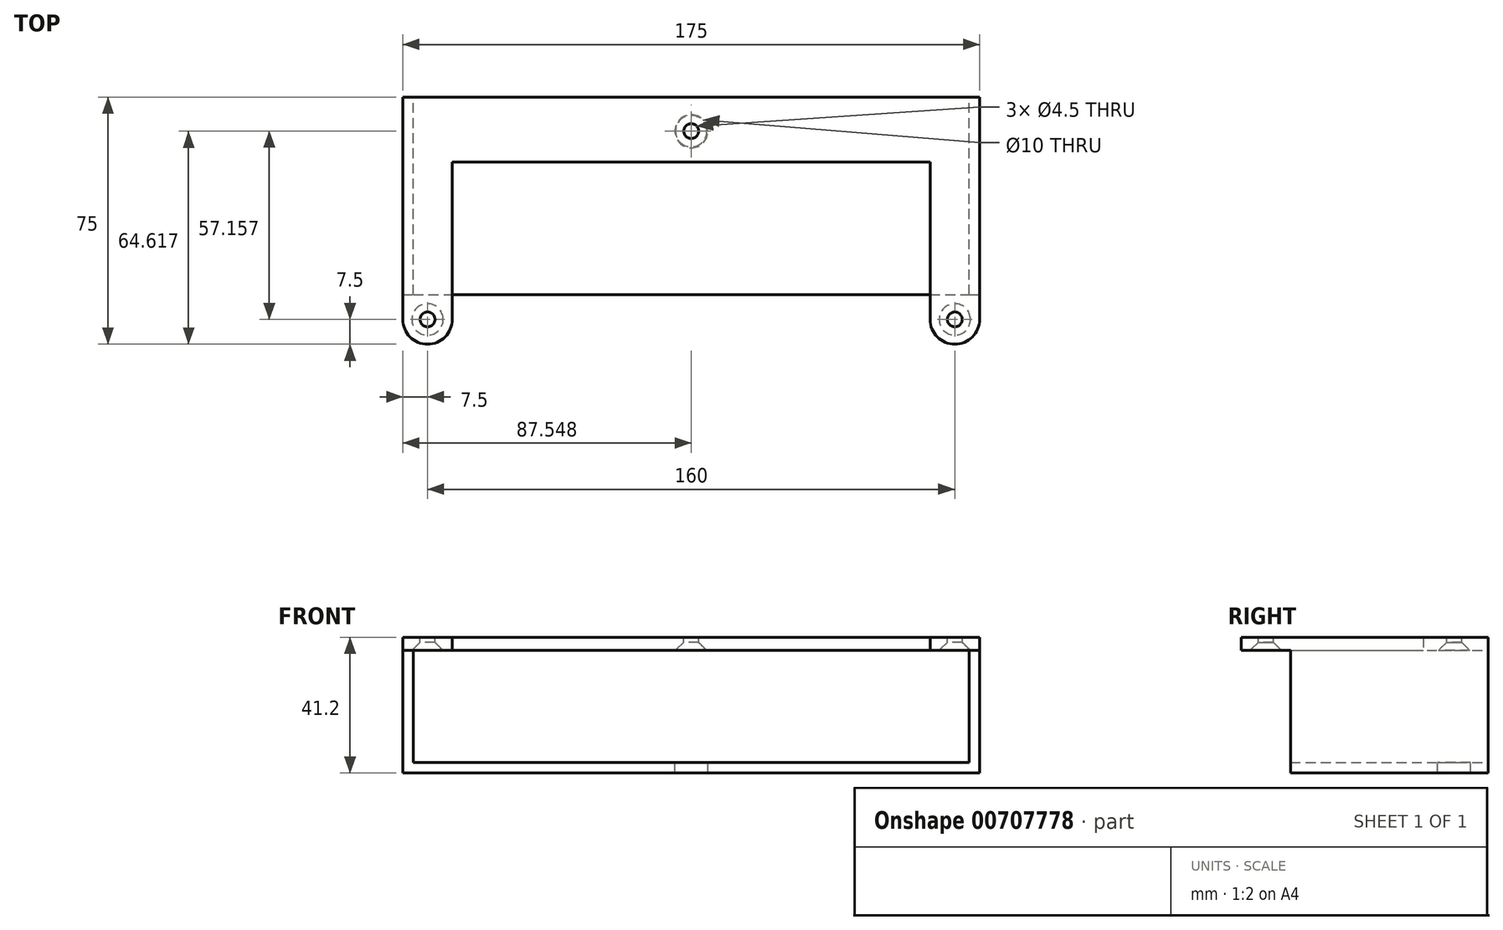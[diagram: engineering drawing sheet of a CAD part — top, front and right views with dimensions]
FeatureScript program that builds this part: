
annotation { "Feature Type Name" : "Feature", "Feature Type Description" : "" }
export const myFeature = defineFeature(function(context is Context, id is Id, definition is map)
    precondition{}
    {
        {
            var Q0;
            Q0=qCreatedBy(makeId("Top.planeOp"),FACE);
            var sketch = newSketch(context, id + "F0", { "sketchPlane" : qUnion([Q0])});
            skLineSegment(sketch, "E0.bottom", {"start": v(0, 0) * mm, "end": v(175, 0) * mm});
            skLineSegment(sketch, "E0.top", {"start": v(0, -60) * mm, "end": v(175, -60) * mm});
            skLineSegment(sketch, "E0.left", {"start": v(0, 0) * mm, "end": v(0, -60) * mm});
            skLineSegment(sketch, "E0.right", {"start": v(175, 0) * mm, "end": v(175, -60) * mm});
            skLineSegment(sketch, "E1", {"start": v(3.2, -60) * mm, "end": v(3.2, 0) * mm});
            skLineSegment(sketch, "E2", {"start": v(171.8, -60) * mm, "end": v(171.8, 0) * mm});
            skSolve(sketch);
        }
        {
            var Q0;
            Q0 = qSketchRegion(id + "F0", true);
            extrude(context, id + "F1", {"entities" : qUnion([Q0]), "depth" : 3 * mm, "offsetDistance" : 25 * mm});
        }
        {
            var Q0;
            {var subQ0=sQuery(id+"F0.wireOp",EDGE,"E0.left");Q0=makeQuery(id+"F0.imprint","IMPRINT",FACE,{"disambiguationData":[TD([[makeQuery(id+"F0.imprint","IMPRINT",EDGE,{"derivedFrom":subQ0}),1.0]])]});}
            var Q1;
            {var subQ0=sQuery(id+"F0.wireOp",EDGE,"E0.right");Q1=makeQuery(id+"F0.imprint","IMPRINT",FACE,{"disambiguationData":[TD([[makeQuery(id+"F0.imprint","IMPRINT",EDGE,{"derivedFrom":subQ0}),-1.0]])]});}
            extrude(context, id + "F2", {"entities" : qUnion([Q0, Q1]), "operationType" : NewBodyOperationType.ADD, "oppositeDirection" : true, "depth" : 37.2 * mm, "offsetDistance" : 25 * mm});
        }
        {
            var Q0;
            Q0=makeQuery(id+"F2.opExtrude","SWEPT_FACE",FACE,{"disambiguationData":[OSD([sQuery(id+"F0.wireOp",EDGE,"E2")])]});
            var sketch = newSketch(context, id + "F3", { "sketchPlane" : qUnion([Q0])});
            skLineSegment(sketch, "E3.bottom", {"start": v(60, -37.2) * mm, "end": v(0, -37.2) * mm});
            skLineSegment(sketch, "E3.top", {"start": v(60, -34) * mm, "end": v(0, -34) * mm});
            skLineSegment(sketch, "E3.left", {"start": v(60, -37.2) * mm, "end": v(60, -34) * mm});
            skLineSegment(sketch, "E3.right", {"start": v(0, -37.2) * mm, "end": v(0, -34) * mm});
            skSolve(sketch);
        }
        {
            var Q0;
            Q0 = qSketchRegion(id + "F3", true);
            var Q1;
            Q1=makeQuery(id+"F2.opExtrude","SWEPT_FACE",FACE,{"disambiguationData":[OSD([sQuery(id+"F0.wireOp",EDGE,"E1")])]});
            extrude(context, id + "F4", {"entities" : qUnion([Q0]), "operationType" : NewBodyOperationType.ADD, "endBound" : BoundingType.UP_TO_SURFACE, "depth" : 25 * mm, "endBoundEntityFace" : qUnion([Q1]), "offsetDistance" : 25 * mm});
        }
        {
            var Q0;
            {var subQ0=sQuery(id+"F0.wireOp",EDGE,"E0.top");Q0=makeQuery(id+"F4.boolean.opBoolean","MERGE",FACE,{"derivedFrom":[makeQuery(id+"F2.boolean.opBoolean","MERGE",FACE,{"derivedFrom":[makeQuery(id+"F1.opExtrude","SWEPT_FACE",FACE,{"disambiguationData":[OSD([subQ0])]}),makeQuery(id+"F2.opExtrude","SWEPT_FACE",FACE,{"disambiguationData":[OSD([subQ0]),TDD([makeQuery(id+"F0.imprint","IMPRINT",EDGE,{"disambiguationData":[TD([[makeQuery(id+"F0.imprint","INTERSECT",VERTEX,{"derivedFrom":[subQ0,sQuery(id+"F0.wireOp",EDGE,"E0.left")]}),-1.0]])],"derivedFrom":subQ0})])]}),makeQuery(id+"F2.opExtrude","SWEPT_FACE",FACE,{"disambiguationData":[OSD([subQ0]),TDD([makeQuery(id+"F0.imprint","IMPRINT",EDGE,{"disambiguationData":[TD([[makeQuery(id+"F0.imprint","INTERSECT",VERTEX,{"derivedFrom":[subQ0,sQuery(id+"F0.wireOp",EDGE,"E0.right")]}),1.0]])],"derivedFrom":subQ0})])]})]}),makeQuery(id+"F4.opExtrude","SWEPT_FACE",FACE,{"disambiguationData":[OSD([sQuery(id+"F3.wireOp",EDGE,"E3.left")])]})]});}
            var sketch = newSketch(context, id + "F5", { "sketchPlane" : qUnion([Q0])});
            skLineSegment(sketch, "E4", {"start": v(87.5, 3) * mm, "end": v(87.5, 0) * mm, "construction": true});
            skLineSegment(sketch, "E5.bottom", {"start": v(0, 3) * mm, "end": v(15, 3) * mm});
            skLineSegment(sketch, "E5.top", {"start": v(0, 0) * mm, "end": v(15, 0) * mm});
            skLineSegment(sketch, "E5.left", {"start": v(0, 3) * mm, "end": v(0, 0) * mm});
            skLineSegment(sketch, "E5.right", {"start": v(15, 3) * mm, "end": v(15, 0) * mm});
            skLineSegment(sketch, "E6.MirrorCS", {"start": v(175, 3) * mm, "end": v(175, 0) * mm});
            skLineSegment(sketch, "E7.MirrorCS", {"start": v(160, 3) * mm, "end": v(160, 0) * mm});
            skLineSegment(sketch, "E8.MirrorCS", {"start": v(175, 3) * mm, "end": v(160, 3) * mm});
            skLineSegment(sketch, "E9.MirrorCS", {"start": v(175, 0) * mm, "end": v(160, 0) * mm});
            skSolve(sketch);
        }
        {
            var Q0;
            Q0 = qSketchRegion(id + "F5", true);
            extrude(context, id + "F6", {"entities" : qUnion([Q0]), "operationType" : NewBodyOperationType.ADD, "depth" : 15 * mm, "offsetDistance" : 25 * mm});
        }
        {
            var Q0;
            {var subQ0=sQuery(id+"F0.wireOp",EDGE,"E0.bottom");Q0=makeQuery(id+"F4.boolean.opBoolean","MERGE",FACE,{"derivedFrom":[makeQuery(id+"F2.boolean.opBoolean","MERGE",FACE,{"derivedFrom":[makeQuery(id+"F1.opExtrude","SWEPT_FACE",FACE,{"disambiguationData":[OSD([subQ0])]}),makeQuery(id+"F2.opExtrude","SWEPT_FACE",FACE,{"disambiguationData":[OSD([subQ0]),TDD([makeQuery(id+"F0.imprint","IMPRINT",EDGE,{"disambiguationData":[TD([[makeQuery(id+"F0.imprint","INTERSECT",VERTEX,{"derivedFrom":[subQ0,sQuery(id+"F0.wireOp",EDGE,"E0.left")]}),-1.0]])],"derivedFrom":subQ0})])]}),makeQuery(id+"F2.opExtrude","SWEPT_FACE",FACE,{"disambiguationData":[OSD([subQ0]),TDD([makeQuery(id+"F0.imprint","IMPRINT",EDGE,{"disambiguationData":[TD([[makeQuery(id+"F0.imprint","INTERSECT",VERTEX,{"derivedFrom":[subQ0,sQuery(id+"F0.wireOp",EDGE,"E0.right")]}),1.0]])],"derivedFrom":subQ0})])]})]}),makeQuery(id+"F4.opExtrude","SWEPT_FACE",FACE,{"disambiguationData":[OSD([sQuery(id+"F3.wireOp",EDGE,"E3.right")])]})]});}
            var sketch = newSketch(context, id + "F7", { "sketchPlane" : qUnion([Q0])});
            skLineSegment(sketch, "E10", {"start": v(-87.5, 3) * mm, "end": v(-87.5, 0) * mm, "construction": true});
            skLineSegment(sketch, "E11.bottom", {"start": v(-175, 3) * mm, "end": v(-160, 3) * mm});
            skLineSegment(sketch, "E11.top", {"start": v(-175, 0) * mm, "end": v(-160, 0) * mm});
            skLineSegment(sketch, "E11.left", {"start": v(-175, 3) * mm, "end": v(-175, 0) * mm});
            skLineSegment(sketch, "E11.right", {"start": v(-160, 3) * mm, "end": v(-160, 0) * mm});
            skLineSegment(sketch, "E12.MirrorCS", {"start": v(0, 3) * mm, "end": v(0, 0) * mm});
            skLineSegment(sketch, "E13.MirrorCS", {"start": v(-15, 3) * mm, "end": v(-15, 0) * mm});
            skLineSegment(sketch, "E14.MirrorCS", {"start": v(0, 3) * mm, "end": v(-15, 3) * mm});
            skLineSegment(sketch, "E15.MirrorCS", {"start": v(0, 0) * mm, "end": v(-15, 0) * mm});
            skSolve(sketch);
        }
        {
            var Q0;
            Q0 = qSketchRegion(id + "F7", true);
            extrude(context, id + "F8", {"entities" : qUnion([Q0]), "operationType" : NewBodyOperationType.ADD, "depth" : 15 * mm, "offsetDistance" : 25 * mm});
        }
        {
            var Q0;
            Q0=makeQuery(id+"F8.boolean.opBoolean","MERGE",FACE,{"derivedFrom":[makeQuery(id+"F6.boolean.opBoolean","MERGE",FACE,{"derivedFrom":[makeQuery(id+"F1.opExtrude","CAP_FACE",FACE,{"disambiguationData":[OSD([sQuery(id+"F0.wireOp",EDGE,"E0.bottom"),sQuery(id+"F0.wireOp",EDGE,"E0.top"),sQuery(id+"F0.wireOp",EDGE,"E0.left"),sQuery(id+"F0.wireOp",EDGE,"E0.right")])],"isStart":false}),makeQuery(id+"F6.opExtrude","SWEPT_FACE",FACE,{"disambiguationData":[OSD([sQuery(id+"F5.wireOp",EDGE,"E5.bottom")])]}),makeQuery(id+"F6.opExtrude","SWEPT_FACE",FACE,{"disambiguationData":[OSD([sQuery(id+"F5.wireOp",EDGE,"E8.MirrorCS")])]})]}),makeQuery(id+"F8.opExtrude","SWEPT_FACE",FACE,{"disambiguationData":[OSD([sQuery(id+"F7.wireOp",EDGE,"E11.bottom")])]}),makeQuery(id+"F8.opExtrude","SWEPT_FACE",FACE,{"disambiguationData":[OSD([sQuery(id+"F7.wireOp",EDGE,"E14.MirrorCS")])]})]});
            var sketch = newSketch(context, id + "F9", { "sketchPlane" : qUnion([Q0])});
            skCircle(sketch, "E16", {"center": v(167.5, 7.5) * mm, "radius": 2.25 * mm});
            skCircle(sketch, "E17", {"center": v(167.5, -67.5) * mm, "radius": 2.25 * mm});
            skCircle(sketch, "E18", {"center": v(7.5, -67.5) * mm, "radius": 2.25 * mm});
            skCircle(sketch, "E19", {"center": v(87.5, -10.34) * mm, "radius": 2.25 * mm});
            skPoint(sketch, "E20", {"position": v(87.5, 0) * mm});
            skSolve(sketch);
        }
        {
            var Q0;
            Q0 = qSketchRegion(id + "F9", true);
            extrude(context, id + "F10", {"entities" : qUnion([Q0]), "operationType" : NewBodyOperationType.REMOVE, "oppositeDirection" : true, "depth" : 25 * mm, "offsetDistance" : 25 * mm});
        }
        {
            var Q0;
            Q0=makeQuery(id+"F8.boolean.opBoolean","MERGE",FACE,{"derivedFrom":[makeQuery(id+"F6.boolean.opBoolean","MERGE",FACE,{"derivedFrom":[makeQuery(id+"F1.opExtrude","CAP_FACE",FACE,{"disambiguationData":[OSD([sQuery(id+"F0.wireOp",EDGE,"E0.bottom"),sQuery(id+"F0.wireOp",EDGE,"E0.top"),sQuery(id+"F0.wireOp",EDGE,"E0.left"),sQuery(id+"F0.wireOp",EDGE,"E0.right")])],"isStart":false}),makeQuery(id+"F6.opExtrude","SWEPT_FACE",FACE,{"disambiguationData":[OSD([sQuery(id+"F5.wireOp",EDGE,"E5.bottom")])]}),makeQuery(id+"F6.opExtrude","SWEPT_FACE",FACE,{"disambiguationData":[OSD([sQuery(id+"F5.wireOp",EDGE,"E8.MirrorCS")])]})]}),makeQuery(id+"F8.opExtrude","SWEPT_FACE",FACE,{"disambiguationData":[OSD([sQuery(id+"F7.wireOp",EDGE,"E11.bottom")])]}),makeQuery(id+"F8.opExtrude","SWEPT_FACE",FACE,{"disambiguationData":[OSD([sQuery(id+"F7.wireOp",EDGE,"E14.MirrorCS")])]})]});
            extrude(context, id + "F11", {"entities" : qUnion([Q0]), "operationType" : NewBodyOperationType.ADD, "depth" : 1 * mm, "offsetDistance" : 25 * mm});
        }
        {
            var Q0;
            Q0=makeQuery(id+"F10.boolean.opBoolean","INTERSECT",EDGE,{"derivedFrom":[makeQuery(id+"F8.boolean.opBoolean","MERGE",FACE,{"derivedFrom":[makeQuery(id+"F6.boolean.opBoolean","MERGE",FACE,{"derivedFrom":[makeQuery(id+"F1.opExtrude","CAP_FACE",FACE,{"disambiguationData":[OSD([sQuery(id+"F0.wireOp",EDGE,"E0.bottom"),sQuery(id+"F0.wireOp",EDGE,"E0.top"),sQuery(id+"F0.wireOp",EDGE,"E0.left"),sQuery(id+"F0.wireOp",EDGE,"E0.right")])],"isStart":true}),makeQuery(id+"F6.opExtrude","SWEPT_FACE",FACE,{"disambiguationData":[OSD([sQuery(id+"F5.wireOp",EDGE,"E5.top")])]}),makeQuery(id+"F6.opExtrude","SWEPT_FACE",FACE,{"disambiguationData":[OSD([sQuery(id+"F5.wireOp",EDGE,"E9.MirrorCS")])]})]}),makeQuery(id+"F8.opExtrude","SWEPT_FACE",FACE,{"disambiguationData":[OSD([sQuery(id+"F7.wireOp",EDGE,"E11.top")])]}),makeQuery(id+"F8.opExtrude","SWEPT_FACE",FACE,{"disambiguationData":[OSD([sQuery(id+"F7.wireOp",EDGE,"E15.MirrorCS")])]})]}),makeQuery(id+"F10.opExtrude","SWEPT_FACE",FACE,{"disambiguationData":[OSD([sQuery(id+"F9.wireOp",EDGE,"E17")])]})]});
            var Q1;
            Q1=makeQuery(id+"F10.boolean.opBoolean","INTERSECT",EDGE,{"derivedFrom":[makeQuery(id+"F8.boolean.opBoolean","MERGE",FACE,{"derivedFrom":[makeQuery(id+"F6.boolean.opBoolean","MERGE",FACE,{"derivedFrom":[makeQuery(id+"F1.opExtrude","CAP_FACE",FACE,{"disambiguationData":[OSD([sQuery(id+"F0.wireOp",EDGE,"E0.bottom"),sQuery(id+"F0.wireOp",EDGE,"E0.top"),sQuery(id+"F0.wireOp",EDGE,"E0.left"),sQuery(id+"F0.wireOp",EDGE,"E0.right")])],"isStart":true}),makeQuery(id+"F6.opExtrude","SWEPT_FACE",FACE,{"disambiguationData":[OSD([sQuery(id+"F5.wireOp",EDGE,"E5.top")])]}),makeQuery(id+"F6.opExtrude","SWEPT_FACE",FACE,{"disambiguationData":[OSD([sQuery(id+"F5.wireOp",EDGE,"E9.MirrorCS")])]})]}),makeQuery(id+"F8.opExtrude","SWEPT_FACE",FACE,{"disambiguationData":[OSD([sQuery(id+"F7.wireOp",EDGE,"E11.top")])]}),makeQuery(id+"F8.opExtrude","SWEPT_FACE",FACE,{"disambiguationData":[OSD([sQuery(id+"F7.wireOp",EDGE,"E15.MirrorCS")])]})]}),makeQuery(id+"F10.opExtrude","SWEPT_FACE",FACE,{"disambiguationData":[OSD([sQuery(id+"F9.wireOp",EDGE,"E16")])]})]});
            var Q2;
            Q2=makeQuery(id+"F10.boolean.opBoolean","INTERSECT",EDGE,{"derivedFrom":[makeQuery(id+"F8.boolean.opBoolean","MERGE",FACE,{"derivedFrom":[makeQuery(id+"F6.boolean.opBoolean","MERGE",FACE,{"derivedFrom":[makeQuery(id+"F1.opExtrude","CAP_FACE",FACE,{"disambiguationData":[OSD([sQuery(id+"F0.wireOp",EDGE,"E0.bottom"),sQuery(id+"F0.wireOp",EDGE,"E0.top"),sQuery(id+"F0.wireOp",EDGE,"E0.left"),sQuery(id+"F0.wireOp",EDGE,"E0.right")])],"isStart":true}),makeQuery(id+"F6.opExtrude","SWEPT_FACE",FACE,{"disambiguationData":[OSD([sQuery(id+"F5.wireOp",EDGE,"E5.top")])]}),makeQuery(id+"F6.opExtrude","SWEPT_FACE",FACE,{"disambiguationData":[OSD([sQuery(id+"F5.wireOp",EDGE,"E9.MirrorCS")])]})]}),makeQuery(id+"F8.opExtrude","SWEPT_FACE",FACE,{"disambiguationData":[OSD([sQuery(id+"F7.wireOp",EDGE,"E11.top")])]}),makeQuery(id+"F8.opExtrude","SWEPT_FACE",FACE,{"disambiguationData":[OSD([sQuery(id+"F7.wireOp",EDGE,"E15.MirrorCS")])]})]}),makeQuery(id+"F10.opExtrude","SWEPT_FACE",FACE,{"disambiguationData":[OSD([sQuery(id+"F9.wireOp",EDGE,"E19")])]})]});
            var Q3;
            Q3=makeQuery(id+"F10.boolean.opBoolean","INTERSECT",EDGE,{"derivedFrom":[makeQuery(id+"F8.boolean.opBoolean","MERGE",FACE,{"derivedFrom":[makeQuery(id+"F6.boolean.opBoolean","MERGE",FACE,{"derivedFrom":[makeQuery(id+"F1.opExtrude","CAP_FACE",FACE,{"disambiguationData":[OSD([sQuery(id+"F0.wireOp",EDGE,"E0.bottom"),sQuery(id+"F0.wireOp",EDGE,"E0.top"),sQuery(id+"F0.wireOp",EDGE,"E0.left"),sQuery(id+"F0.wireOp",EDGE,"E0.right")])],"isStart":true}),makeQuery(id+"F6.opExtrude","SWEPT_FACE",FACE,{"disambiguationData":[OSD([sQuery(id+"F5.wireOp",EDGE,"E5.top")])]}),makeQuery(id+"F6.opExtrude","SWEPT_FACE",FACE,{"disambiguationData":[OSD([sQuery(id+"F5.wireOp",EDGE,"E9.MirrorCS")])]})]}),makeQuery(id+"F8.opExtrude","SWEPT_FACE",FACE,{"disambiguationData":[OSD([sQuery(id+"F7.wireOp",EDGE,"E11.top")])]}),makeQuery(id+"F8.opExtrude","SWEPT_FACE",FACE,{"disambiguationData":[OSD([sQuery(id+"F7.wireOp",EDGE,"E15.MirrorCS")])]})]}),makeQuery(id+"F10.opExtrude","SWEPT_FACE",FACE,{"disambiguationData":[OSD([sQuery(id+"F9.wireOp",EDGE,"E18")])]})]});
            chamfer(context, id + "F12", {"entities" : qUnion([Q0, Q1, Q2, Q3]), "width" : 2.5 * mm, "tangentPropagation" : true});
        }
        {
            var Q0;
            {var subQ0=sQuery(id+"F7.wireOp",EDGE,"E12.MirrorCS");var subQ1=sQuery(id+"F5.wireOp",EDGE,"E5.left");var subQ2=sQuery(id+"F0.wireOp",EDGE,"E0.left");Q0=makeQuery(id+"F11.boolean.opBoolean","MERGE",FACE,{"derivedFrom":[makeQuery(id+"F8.boolean.opBoolean","MERGE",FACE,{"derivedFrom":[makeQuery(id+"F6.boolean.opBoolean","MERGE",FACE,{"derivedFrom":[makeQuery(id+"F2.boolean.opBoolean","MERGE",FACE,{"derivedFrom":[makeQuery(id+"F1.opExtrude","SWEPT_FACE",FACE,{"disambiguationData":[OSD([subQ2])]}),makeQuery(id+"F2.opExtrude","SWEPT_FACE",FACE,{"disambiguationData":[OSD([subQ2])]})]}),makeQuery(id+"F6.opExtrude","SWEPT_FACE",FACE,{"disambiguationData":[OSD([subQ1])]})]}),makeQuery(id+"F8.opExtrude","SWEPT_FACE",FACE,{"disambiguationData":[OSD([subQ0])]})]}),makeQuery(id+"F11.opExtrude","SWEPT_FACE",FACE,{"disambiguationData":[OSD([subQ2,sQuery(id+"F5.wireOp",EDGE,"E5.bottom"),subQ1,subQ0,sQuery(id+"F7.wireOp",EDGE,"E14.MirrorCS")])]})]});}
            var sketch = newSketch(context, id + "F13", { "sketchPlane" : qUnion([Q0])});
            skLineSegment(sketch, "E21.bottom", {"start": v(0, 0) * mm, "end": v(-35.82, 0) * mm});
            skLineSegment(sketch, "E21.top", {"start": v(0, 13.56) * mm, "end": v(-35.82, 13.56) * mm});
            skLineSegment(sketch, "E21.left", {"start": v(0, 0) * mm, "end": v(0, 13.56) * mm});
            skLineSegment(sketch, "E21.right", {"start": v(-35.82, 0) * mm, "end": v(-35.82, 13.56) * mm});
            skSolve(sketch);
        }
        {
            var Q0;
            Q0 = qSketchRegion(id + "F13", true);
            extrude(context, id + "F14", {"entities" : qUnion([Q0]), "operationType" : NewBodyOperationType.REMOVE, "endBound" : BoundingType.THROUGH_ALL, "oppositeDirection" : true, "depth" : 25 * mm, "offsetDistance" : 25 * mm});
        }
        {
            var Q0;
            Q0=makeQuery(id+"F4.opExtrude","SWEPT_FACE",FACE,{"disambiguationData":[OSD([sQuery(id+"F3.wireOp",EDGE,"E3.top")])]});
            var sketch = newSketch(context, id + "F15", { "sketchPlane" : qUnion([Q0])});
            skCircle(sketch, "E22", {"center": v(87.55, -10.38) * mm, "radius": 5 * mm});
            skSolve(sketch);
        }
        {
            var Q0;
            Q0 = qSketchRegion(id + "F15", true);
            extrude(context, id + "F16", {"entities" : qUnion([Q0]), "operationType" : NewBodyOperationType.REMOVE, "oppositeDirection" : true, "depth" : 25 * mm, "offsetDistance" : 25 * mm});
        }
        {
            var Q0;
            Q0=makeQuery(id+"F8.opExtrude","CAP_EDGE",EDGE,{"disambiguationData":[OSD([sQuery(id+"F7.wireOp",EDGE,"E11.left")])],"isStart":false});
            var Q1;
            Q1=makeQuery(id+"F8.opExtrude","CAP_EDGE",EDGE,{"disambiguationData":[OSD([sQuery(id+"F7.wireOp",EDGE,"E11.right")])],"isStart":false});
            var Q2;
            Q2=makeQuery(id+"F8.opExtrude","CAP_EDGE",EDGE,{"disambiguationData":[OSD([sQuery(id+"F7.wireOp",EDGE,"E13.MirrorCS")])],"isStart":false});
            var Q3;
            Q3=makeQuery(id+"F8.opExtrude","CAP_EDGE",EDGE,{"disambiguationData":[OSD([sQuery(id+"F7.wireOp",EDGE,"E12.MirrorCS")])],"isStart":false});
            var Q4;
            Q4=makeQuery(id+"F8.opExtrude","CAP_EDGE",EDGE,{"disambiguationData":[OSD([sQuery(id+"F7.wireOp",EDGE,"E13.MirrorCS")])],"isStart":true});
            var Q5;
            Q5=makeQuery(id+"F8.opExtrude","CAP_EDGE",EDGE,{"disambiguationData":[OSD([sQuery(id+"F7.wireOp",EDGE,"E11.right")])],"isStart":true});
            var Q6;
            Q6=makeQuery(id+"F6.opExtrude","CAP_EDGE",EDGE,{"disambiguationData":[OSD([sQuery(id+"F5.wireOp",EDGE,"E5.right")])],"isStart":false});
            var Q7;
            Q7=makeQuery(id+"F6.opExtrude","CAP_EDGE",EDGE,{"disambiguationData":[OSD([sQuery(id+"F5.wireOp",EDGE,"E5.left")])],"isStart":false});
            var Q8;
            Q8=makeQuery(id+"F6.opExtrude","CAP_EDGE",EDGE,{"disambiguationData":[OSD([sQuery(id+"F5.wireOp",EDGE,"E7.MirrorCS")])],"isStart":false});
            var Q9;
            Q9=makeQuery(id+"F6.opExtrude","CAP_EDGE",EDGE,{"disambiguationData":[OSD([sQuery(id+"F5.wireOp",EDGE,"E6.MirrorCS")])],"isStart":false});
            fillet(context, id + "F17", {"entities" : qUnion([Q0, Q1, Q2, Q3, Q4, Q5, Q6, Q7, Q8, Q9]), "radius" : 7.5 * mm, "tangentPropagation" : true, "allowEdgeOverflow" : false});
        }
        {
            var Q0;
            {var subQ0=sQuery(id+"F0.wireOp",EDGE,"E0.top");var subQ1=sQuery(id+"F0.wireOp",EDGE,"E0.right");var subQ2=sQuery(id+"F0.wireOp",EDGE,"E0.left");Q0=makeQuery(id+"F11.boolean.opBoolean","MERGE",FACE,{"derivedFrom":[makeQuery(id+"F6.boolean.opBoolean","SPLIT",FACE,{"disambiguationData":[TD([makeQuery(id+"F6.opExtrude","SWEPT_FACE",FACE,{"disambiguationData":[OSD([sQuery(id+"F5.wireOp",EDGE,"E5.bottom")])]})])],"derivedFrom":makeQuery(id+"F4.boolean.opBoolean","MERGE",FACE,{"derivedFrom":[makeQuery(id+"F2.boolean.opBoolean","MERGE",FACE,{"derivedFrom":[makeQuery(id+"F1.opExtrude","SWEPT_FACE",FACE,{"disambiguationData":[OSD([subQ0])]}),makeQuery(id+"F2.opExtrude","SWEPT_FACE",FACE,{"disambiguationData":[OSD([subQ0]),TDD([makeQuery(id+"F0.imprint","IMPRINT",EDGE,{"disambiguationData":[TD([[makeQuery(id+"F0.imprint","INTERSECT",VERTEX,{"derivedFrom":[subQ0,subQ2]}),-1.0]])],"derivedFrom":subQ0})])]}),makeQuery(id+"F2.opExtrude","SWEPT_FACE",FACE,{"disambiguationData":[OSD([subQ0]),TDD([makeQuery(id+"F0.imprint","IMPRINT",EDGE,{"disambiguationData":[TD([[makeQuery(id+"F0.imprint","INTERSECT",VERTEX,{"derivedFrom":[subQ0,subQ1]}),1.0]])],"derivedFrom":subQ0})])]})]}),makeQuery(id+"F4.opExtrude","SWEPT_FACE",FACE,{"disambiguationData":[OSD([sQuery(id+"F3.wireOp",EDGE,"E3.left")])]})]})}),makeQuery(id+"F11.opExtrude","SWEPT_FACE",FACE,{"disambiguationData":[OSD([subQ0])]})]});}
            extrude(context, id + "F18", {"entities" : qUnion([Q0]), "operationType" : NewBodyOperationType.REMOVE, "oppositeDirection" : true, "depth" : 40.3 * mm, "offsetDistance" : 25 * mm});
        }
    });
